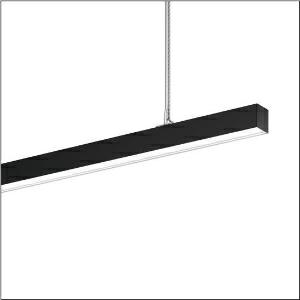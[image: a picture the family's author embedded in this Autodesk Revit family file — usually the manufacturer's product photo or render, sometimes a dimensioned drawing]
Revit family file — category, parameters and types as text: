
# Revit family: silica_r__21_51mx30tat4b_500a
name_source: partatom
category: Lighting Fixtures
units: mm (PartAtom-declared; Revit-internal decimal feet)

## family parameters
Cut with Voids When Loaded = No
Host = Face
Light Source = No
Part Type = Normal
Room Calculation Point = No
Round Connector Dimension = Use Diameter
Shared = No

## types (1)
- --- (1 x LED, 4120 lm, 33.8 W, 6500K)
    Apparent Load = 34 VA
    CIE Flux Codes = 47 79 96 58 100
    Color Rendering = 80
    Color Temperature = 6500K
    Default Elevation = 1800 mm
    Description = Silica® 21, office luminaire, primary optical cover: cover, of PMMA, opal, light emission: direct/indirect distribution, primary light characteristic: symmetric, installation type: suspended mounting, LED, rated luminous flux: 4.120lm, luminous efficacy: 116lm/W, light colour: 8tw, colour temperature: 2700..6500K, control gear: ECG DALI, with terminal, 3+2-pole, max. 2.5mm², mains connection: 220..240V, AC, 50/60Hz, rated input power: 35.5W, luminaire housing, of aluminium, jet black (RAL 9005), length: 1.204mm, width: 53mm, height: 53mm, protection rating (complete): IP20, insulation class (complete): insulation class I (protective earthing), certification: CE, permissible operating ambient temperature: 0..+35°C, standard: EN 50419, packaging unit: 1 piece
    Height = 53 mm
    Lamp = 1 x LED
    Lamp Light Flux = 4120 lm
    Lamp Power = 33.8 W
    Lamp count = 1
    Length = 1204 mm
    Luminous efficacy = 122 lm/W
    Manufacturer = Siteco
    ModVariant = No
    Model = 51MX30TAT4B
    Mounting Place = Ceiling
    Mounting Type = Pendant
    Number of Poles = 1
    OnlyDefault = Yes
    Power Factor = 1
    Product Name = Silica® 21
    Product group = office luminaire | ceiling pendant
    ProductGroupID = 902
    Protection Class = Protection class I
    Protection Degree = IP 20
    RLX_Detail_Level = 1
    RLX_Emergency_Light_Flux = 0 lm
    RLX_Emergency_Type = 0
    RLX_Emergency_Type_DB = No
    RlxData = <blob elided: 22853 chars, md5=e5be8345>
    Socket = socket
    Standby Power = 0 W
    System Light Flux = 4120 lm
    System Power = 34 W
    Type Comments = individual setting
    Type Image = l_1313646.jpg
    URL = http://relux.com
    VarID = @adj_089007
    Voltage = 0 V
    Weight = 0.00 kg
    Width = 53 mm

## geometry (parser evidence)
native form markers: Blend x4, Sweep x11
no freeform markers — native parametric forms only
